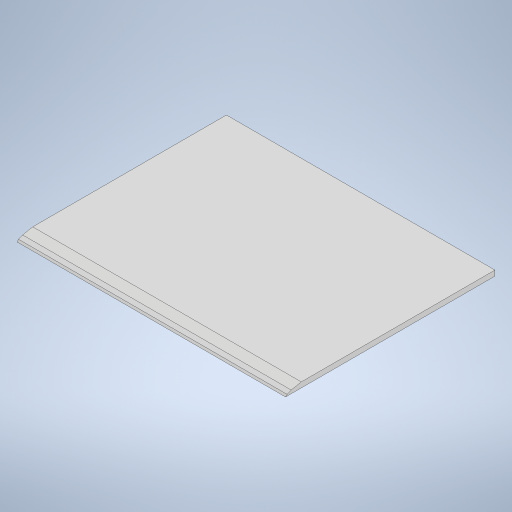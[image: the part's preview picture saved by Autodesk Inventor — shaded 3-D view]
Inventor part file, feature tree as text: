
AUTODESK INVENTOR PART (.ipt)
format: ipt  version: 2024 (Build 280153000, 153)  size: 227,840 bytes
history: native  units: mm
features: chamfer x3, extrude x2, sketch x2
ambient origin geometry x8: Origin, YZ Plane, XZ Plane, XY Plane, X Axis, Y Axis, Z Axis, Center Point
bodies: Solid1 (feature_tree)
feature tree (7):
  extrude  "Extrusion1"  Depth=2.0mm
  chamfer  "Chamfer1"  Distance=2.0mm
  chamfer  "Chamfer2"  Distance=2.0mm Angle=45.0deg
  chamfer  "Chamfer3"  Distance=2.0mm Angle=45.0deg
  extrude  "Extrusion2"  Depth=2.0mm TaperAngle=0.0deg
  sketch  "Sketch1"  dims[d0=102.6mm d1=50.0mm d2=2.0mm d3=0.0mm d4=2.0mm d5=2.0mm d6=45.0deg d7=2.0mm d8=2.0mm d9=45.0deg]
  sketch  "Sketch2"  dims[d10=2.0mm d11=2.0mm d12=45.0deg d13=30.0mm d14=0.0mm]
